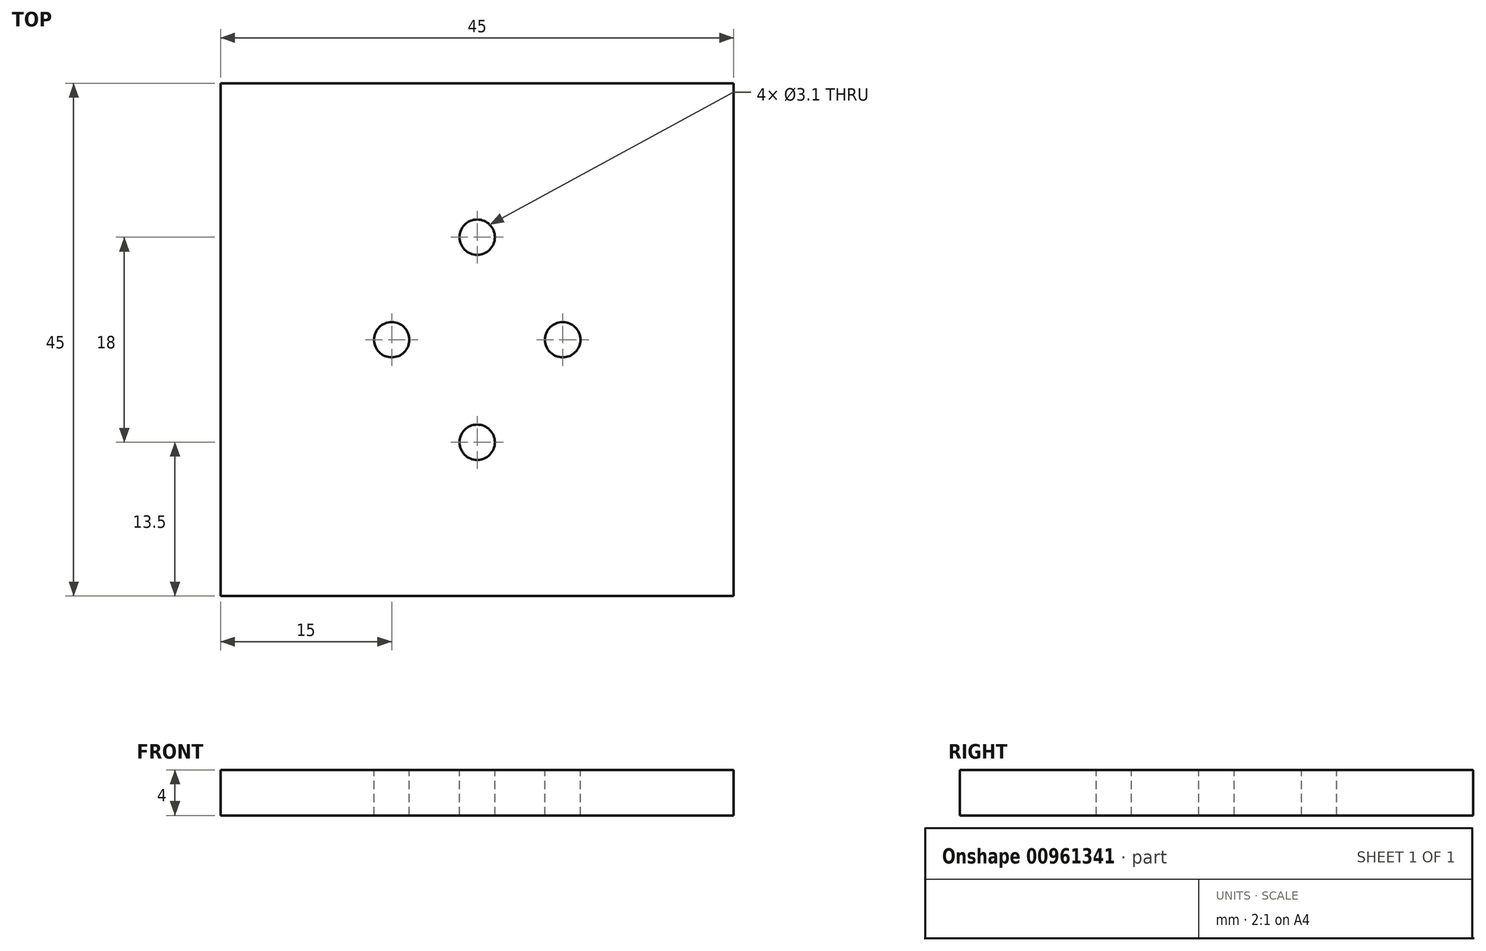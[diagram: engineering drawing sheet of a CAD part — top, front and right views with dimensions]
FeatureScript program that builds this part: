
annotation { "Feature Type Name" : "Feature", "Feature Type Description" : "" }
export const myFeature = defineFeature(function(context is Context, id is Id, definition is map)
    precondition{}
    {
        {
            var Q0;
            Q0=qCreatedBy(makeId("Top.planeOp"),FACE);
            var sketch = newSketch(context, id + "F0", { "sketchPlane" : qUnion([Q0])});
            skLineSegment(sketch, "E0.bottom", {"start": v(22.5, -22.5) * mm, "end": v(-22.5, -22.5) * mm});
            skLineSegment(sketch, "E0.top", {"start": v(22.5, 22.5) * mm, "end": v(-22.5, 22.5) * mm});
            skLineSegment(sketch, "E0.left", {"start": v(22.5, -22.5) * mm, "end": v(22.5, 22.5) * mm});
            skLineSegment(sketch, "E0.right", {"start": v(-22.5, -22.5) * mm, "end": v(-22.5, 22.5) * mm});
            skPoint(sketch, "E0.middle", {"position": v(0, 0) * mm});
            skSolve(sketch);
        }
        {
            var Q0;
            Q0=makeQuery(id+"F0.imprint","IMPRINT",FACE,{"disambiguationData":[TD([[makeQuery(id+"F0.imprint","IMPRINT",EDGE,{"derivedFrom":sQuery(id+"F0.wireOp",EDGE,"E0.bottom")}),-1.0]])]});
            extrude(context, id + "F1", {"entities" : qUnion([Q0]), "depth" : 4 * mm, "offsetDistance" : 25 * mm});
        }
        {
            var Q0;
            Q0=makeQuery(id+"F1.opExtrude","CAP_FACE",FACE,{"disambiguationData":[OSD([sQuery(id+"F0.wireOp",EDGE,"E0.bottom"),sQuery(id+"F0.wireOp",EDGE,"E0.top"),sQuery(id+"F0.wireOp",EDGE,"E0.left"),sQuery(id+"F0.wireOp",EDGE,"E0.right")])],"isStart":false});
            var sketch = newSketch(context, id + "F2", { "sketchPlane" : qUnion([Q0])});
            skLineSegment(sketch, "E1", {"start": v(0, 0) * mm, "end": v(7.5, 0) * mm});
            skLineSegment(sketch, "E2", {"start": v(7.5, 0) * mm, "end": v(0, 0) * mm});
            skLineSegment(sketch, "E3", {"start": v(0, 0) * mm, "end": v(-7.5, 0) * mm});
            skLineSegment(sketch, "E4", {"start": v(0, 0) * mm, "end": v(0, 9) * mm});
            skLineSegment(sketch, "E5", {"start": v(0, 0) * mm, "end": v(0, -9) * mm});
            skPoint(sketch, "E6", {"position": v(0, 9) * mm});
            skPoint(sketch, "E7", {"position": v(-7.5, 0) * mm});
            skPoint(sketch, "E8", {"position": v(0, -9) * mm});
            skPoint(sketch, "E9", {"position": v(7.5, 0) * mm});
            skSolve(sketch);
        }
        {
            var Q0;
            Q0=sQuery(id+"F2.wireOp",VERTEX,"E6");
            var Q1;
            Q1=sQuery(id+"F2.wireOp",VERTEX,"E7");
            var Q2;
            Q2=sQuery(id+"F2.wireOp",VERTEX,"E8");
            var Q3;
            Q3=sQuery(id+"F2.wireOp",VERTEX,"E9");
            var Q4;
            Q4=makeQuery(id+"F1.opExtrude","SWEPT_BODY",BODY,{"disambiguationData":[OSD([sQuery(id+"F0.wireOp",EDGE,"E0.bottom"),sQuery(id+"F0.wireOp",EDGE,"E0.top"),sQuery(id+"F0.wireOp",EDGE,"E0.left"),sQuery(id+"F0.wireOp",EDGE,"E0.right")])]});
            hole(context, id + "F3", {"style" : HoleStyle.SIMPLE, "endStyle" : HoleEndStyle.THROUGH, "holeDiameter" : 3.1 * mm, "majorDiameter" : 5 * mm, "isTappedThrough" : true, "tappedDepth" : 12 * mm, "tapClearance" : 3, "startFromSketch" : true, "locations" : qUnion([Q0, Q1, Q2, Q3]), "scope" : qUnion([Q4])});
        }
    });
